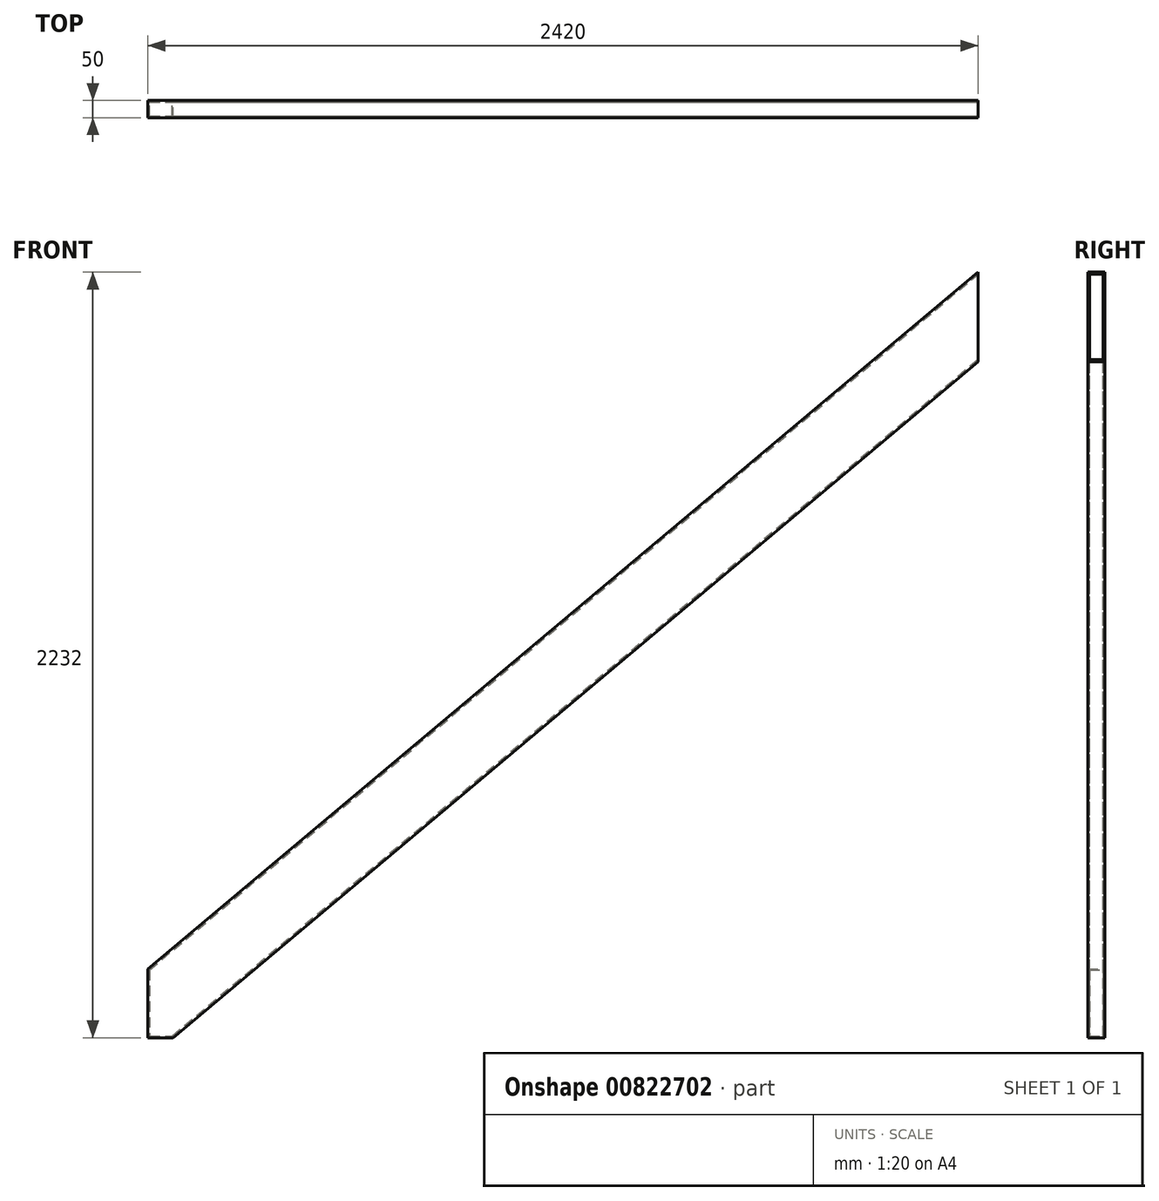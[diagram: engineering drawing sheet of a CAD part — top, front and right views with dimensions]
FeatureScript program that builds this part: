
annotation { "Feature Type Name" : "Feature", "Feature Type Description" : "" }
export const myFeature = defineFeature(function(context is Context, id is Id, definition is map)
    precondition{}
    {
        {
            var Q0;
            Q0=qCreatedBy(makeId("Front.planeOp"),FACE);
            var sketch = newSketch(context, id + "F0", { "sketchPlane" : qUnion([Q0])});
            skLineSegment(sketch, "E0", {"start": v(0, 200) * mm, "end": v(2420, 2232) * mm});
            skLineSegment(sketch, "E1.0", {"start": v(72.83, 0) * mm, "end": v(2420, 1970.85) * mm});
            skLineSegment(sketch, "E2", {"start": v(2420, 2232) * mm, "end": v(2420, 1970.85) * mm});
            skLineSegment(sketch, "E3", {"start": v(0, 200) * mm, "end": v(0, 0) * mm});
            skLineSegment(sketch, "E4", {"start": v(0, 0) * mm, "end": v(72.83, 0) * mm});
            skSolve(sketch);
        }
        {
            var Q0;
            Q0 = qSketchRegion(id + "F0", true);
            extrude(context, id + "F1", {"entities" : qUnion([Q0]), "depth" : 50 * mm, "offsetDistance" : 25 * mm});
        }
        {
            var Q0;
            Q0=makeQuery(id+"F1.opExtrude","SWEPT_FACE",FACE,{"disambiguationData":[OSD([sQuery(id+"F0.wireOp",EDGE,"E2")])]});
            var Q1;
            Q1=makeQuery(id+"F1.opExtrude","SWEPT_BODY",BODY,{"disambiguationData":[OSD([sQuery(id+"F0.wireOp",EDGE,"E0"),sQuery(id+"F0.wireOp",EDGE,"E1.0"),sQuery(id+"F0.wireOp",EDGE,"E2"),sQuery(id+"F0.wireOp",EDGE,"E3"),sQuery(id+"F0.wireOp",EDGE,"E4")])]});
            shell(context, id + "F2", {"entities" : qUnion([Q0]), "parts" : qUnion([Q1]), "thickness" : 5 * mm});
        }
    });
